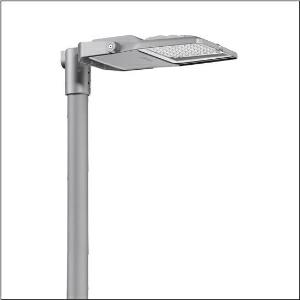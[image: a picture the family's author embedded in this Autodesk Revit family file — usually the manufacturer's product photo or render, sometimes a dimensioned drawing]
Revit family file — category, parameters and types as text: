
# Revit family: floodlight_fl_21_iq_mini___pl61_5xa7772b4c3a_beff
name_source: partatom
category: Lighting Fixtures
units: mm (PartAtom-declared; Revit-internal decimal feet)

## family parameters
Cut with Voids When Loaded = No
Host = Face
Light Source = No
Part Type = Normal
Room Calculation Point = No
Round Connector Dimension = Use Diameter
Shared = No

## types (1)
- --- (1 x LED, 6370 lm, 45.5 W, 4000K)
    Apparent Load = 46 VA
    CIE Flux Codes = 33 65 98 100 100
    Color Rendering = 70
    Color Temperature = 4000K
    Default Elevation = 1800 mm
    Description = Floodlight FL 21 iQ mini, floodlight, primary light control with lens, of PMMA, primary optical cover: protective disc, of toughened safety glass, transparent, light distribution: PL61, light emission: direct distribution, installation type: surface-mounted, LED, High Power LED, rated luminous flux: 6.370lm, luminous efficacy: 140lm/W, light colour: 740, colour temperature: 4000K, control: Auto-Match, Temp-Guard, Night-Set, Smart-Wire, Desk-Remote (wireless, voltage-free reading and setting of iQ features in the workshop via application-optimized NFC function/RFID function), optimised constant luminous flux control (CLO 2.0), Light-Fading, Lumen-Switch, with terminal, 6-pole, mains connection: 220..240V, AC, 50/60Hz, start of lifetime: 46W, end of service life: 48W, reduction: 22W, luminaire housing, of diecast aluminium, powder-coated, Siteco® metallic grey (DB 702S), corrosivity category C5 mid according to DIN EN ISO 12944, sealing non-destructively replaceable, please order mast flange separately, mast bracket, of steel, galvanised, powder-coated, protection rating (complete): IP66, insulation class (complete): insulation class II (safety insulation), certification: CE, ENEC, VDE, protection symbol: D, impact resistance: IK08, permissible operating ambient temperature: -40..+40°C, permissible operating ambient temperature for outdoor applications: -40..+50°C, standard: DIN EN 12944, LABS conformity tested according to VDMA 24364:2018-05, packaging unit: 1 piece

Light Distribution: PL61
    Height = 70 mm
    Lamp = 1 x LED
    Lamp Light Flux = 6370 lm
    Lamp Power = 45.5 W
    Lamp count = 1
    Length = 485 mm
    Luminous efficacy = 140 lm/W
    Manufacturer = Siteco
    ModVariant = No
    Model = 5XA7772B4C3A
    Number of Poles = 1
    OnlyDefault = Yes
    Power Factor = 1
    Product Name = Floodlight FL 21 iQ mini | PL61
    Product group = floodlight | pylon annexe
    ProductGroupID = 6200
    Protection Class = Protection class II
    Protection Degree = IP 66
    RLX_Detail_Level = 1
    RLX_Emergency_Light_Flux = 0 lm
    RLX_Emergency_Type = 0
    RLX_Emergency_Type_DB = No
    RlxData = <blob elided: 101273 chars, md5=50be5985>
    Socket = socket
    Standby Power = 0 W
    System Light Flux = 6370 lm
    System Power = 46 W
    Type Comments = factory setting: luminous flux: 100 % | dim-lin: 254 | 463 mA
    Type Image = l_1007125.jpg
    URL = http://relux.com
    VarID = @adj_106515
    Voltage = 0 V
    Weight = 0.00 kg
    Width = 337 mm

## geometry (parser evidence)
native form markers: Blend x4, Sweep x11
no freeform markers — native parametric forms only
